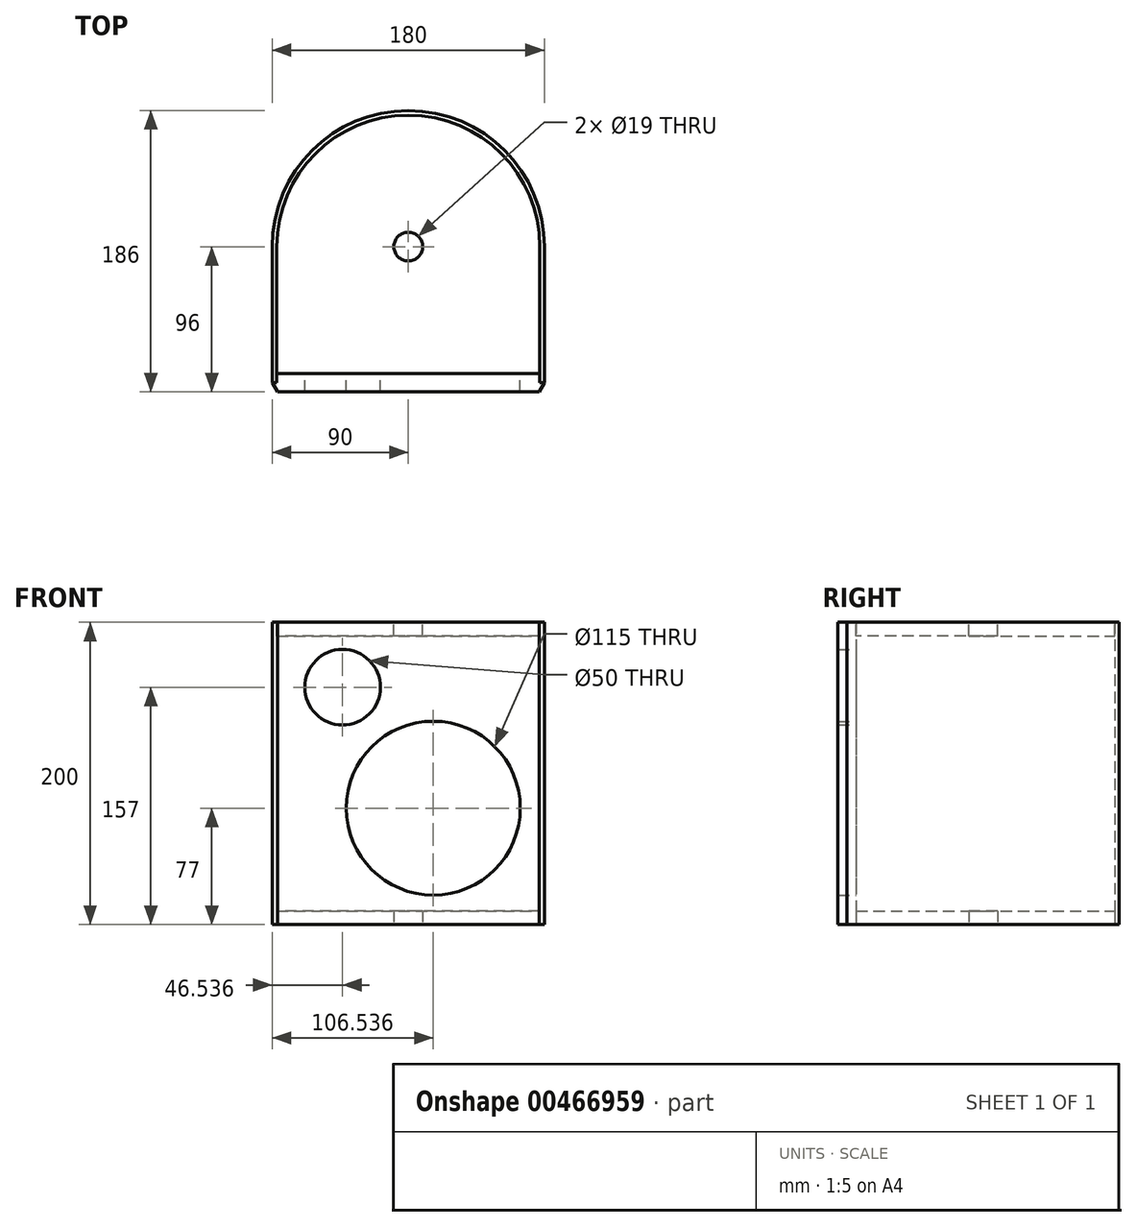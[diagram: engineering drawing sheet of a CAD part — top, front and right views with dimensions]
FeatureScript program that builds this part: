
annotation { "Feature Type Name" : "Feature", "Feature Type Description" : "" }
export const myFeature = defineFeature(function(context is Context, id is Id, definition is map)
    precondition{}
    {
        {
            var Q0;
            Q0=qCreatedBy(makeId("Top.planeOp"),FACE);
            var sketch = newSketch(context, id + "F0", { "sketchPlane" : qUnion([Q0])});
            skArc(sketch, "E0", {"start": v(90, 0) * mm, "mid": v(0, 90) * mm, "end": v(-90, 0) * mm});
            skLineSegment(sketch, "E1", {"start": v(-90, 0) * mm, "end": v(-90, -90) * mm});
            skLineSegment(sketch, "E2", {"start": v(-90, -90) * mm, "end": v(90, -90) * mm});
            skLineSegment(sketch, "E3", {"start": v(90, -90) * mm, "end": v(90, 0) * mm});
            skSolve(sketch);
        }
        {
            var Q0;
            Q0 = qSketchRegion(id + "F0", true);
            extrude(context, id + "F1", {"entities" : qUnion([Q0]), "depth" : 200 * mm});
        }
        {
            var Q0;
            Q0=makeQuery(id+"F1.opExtrude","CAP_FACE",FACE,{"disambiguationData":[OSD([sQuery(id+"F0.wireOp",EDGE,"E0"),sQuery(id+"F0.wireOp",EDGE,"E1"),sQuery(id+"F0.wireOp",EDGE,"E2"),sQuery(id+"F0.wireOp",EDGE,"E3")])],"isStart":false});
            var Q1;
            Q1=makeQuery(id+"F1.opExtrude","SWEPT_FACE",FACE,{"disambiguationData":[OSD([sQuery(id+"F0.wireOp",EDGE,"E2")])]});
            var Q2;
            Q2=makeQuery(id+"F1.opExtrude","CAP_FACE",FACE,{"disambiguationData":[OSD([sQuery(id+"F0.wireOp",EDGE,"E0"),sQuery(id+"F0.wireOp",EDGE,"E1"),sQuery(id+"F0.wireOp",EDGE,"E2"),sQuery(id+"F0.wireOp",EDGE,"E3")])],"isStart":true});
            shell(context, id + "F2", {"entities" : qUnion([Q0, Q1, Q2]), "thickness" : 3 * mm});
        }
        {
            var Q0;
            Q0=qCreatedBy(makeId("Top.planeOp"),FACE);
            var sketch = newSketch(context, id + "F3", { "sketchPlane" : qUnion([Q0])});
            skLineSegment(sketch, "E4", {"start": v(-87, -84) * mm, "end": v(87, -84) * mm});
            skLineSegment(sketch, "E5", {"start": v(87, -84) * mm, "end": v(87, -90) * mm});
            skLineSegment(sketch, "E6", {"start": v(87, -90) * mm, "end": v(90, -90) * mm});
            skLineSegment(sketch, "E7", {"start": v(90, -90) * mm, "end": v(86.54, -96) * mm});
            skLineSegment(sketch, "E8", {"start": v(86.54, -96) * mm, "end": v(-86.54, -96) * mm});
            skLineSegment(sketch, "E9", {"start": v(-86.54, -96) * mm, "end": v(-90, -90) * mm});
            skLineSegment(sketch, "E10", {"start": v(-90, -90) * mm, "end": v(-87, -90) * mm});
            skLineSegment(sketch, "E11", {"start": v(-87, -90) * mm, "end": v(-87, -84) * mm});
            skSolve(sketch);
        }
        {
            var Q0;
            Q0 = qSketchRegion(id + "F3", true);
            var Q1;
            Q1=makeQuery(id+"F1.opExtrude","CAP_FACE",FACE,{"disambiguationData":[OSD([sQuery(id+"F0.wireOp",EDGE,"E0"),sQuery(id+"F0.wireOp",EDGE,"E1"),sQuery(id+"F0.wireOp",EDGE,"E2"),sQuery(id+"F0.wireOp",EDGE,"E3")])],"isStart":false});
            extrude(context, id + "F4", {"entities" : qUnion([Q0]), "endBound" : BoundingType.UP_TO_SURFACE, "endBoundEntityFace" : qUnion([Q1]), "depth" : 25 * mm});
        }
        {
            var Q0;
            Q0=qCreatedBy(makeId("Front.planeOp"),FACE);
            var sketch = newSketch(context, id + "F5", { "sketchPlane" : qUnion([Q0])});
            skCircle(sketch, "E12", {"center": v(16.54, 77) * mm, "radius": 57.5 * mm});
            skCircle(sketch, "E13", {"center": v(-43.46, 157) * mm, "radius": 25 * mm});
            skSolve(sketch);
        }
        {
            var Q0;
            Q0 = qSketchRegion(id + "F5", true);
            extrude(context, id + "F6", {"entities" : qUnion([Q0]), "operationType" : NewBodyOperationType.REMOVE, "endBound" : BoundingType.THROUGH_ALL, "depth" : 25 * mm});
        }
        {
            var Q0;
            Q0=makeQuery(id+"F4.opExtrude","CAP_FACE",FACE,{"disambiguationData":[OSD([sQuery(id+"F3.wireOp",EDGE,"E4"),sQuery(id+"F3.wireOp",EDGE,"E5"),sQuery(id+"F3.wireOp",EDGE,"E6"),sQuery(id+"F3.wireOp",EDGE,"E7"),sQuery(id+"F3.wireOp",EDGE,"E8"),sQuery(id+"F3.wireOp",EDGE,"E9"),sQuery(id+"F3.wireOp",EDGE,"E10"),sQuery(id+"F3.wireOp",EDGE,"E11")])],"isStart":false});
            var sketch = newSketch(context, id + "F7", { "sketchPlane" : qUnion([Q0])});
            skLineSegment(sketch, "E14.0", {"start": v(-87, 0) * mm, "end": v(-87, -84) * mm});
            skArc(sketch, "E15.0", {"start": v(87, 0) * mm, "mid": v(0, 87) * mm, "end": v(-87, 0) * mm});
            skLineSegment(sketch, "E16.0", {"start": v(87, -84) * mm, "end": v(87, 0) * mm});
            skLineSegment(sketch, "E17.0", {"start": v(-87, -84) * mm, "end": v(87, -84) * mm});
            skPoint(sketch, "E18.orphan", {"position": v(-87, -90) * mm});
            skPoint(sketch, "E19.orphan", {"position": v(87, -90) * mm});
            skCircle(sketch, "E20", {"center": v(0, 0) * mm, "radius": 9.5 * mm});
            skSolve(sketch);
        }
        {
            var Q0;
            Q0 = qSketchRegion(id + "F7", true);
            extrude(context, id + "F8", {"entities" : qUnion([Q0]), "oppositeDirection" : true, "depth" : 9 * mm});
        }
        {
            var Q0;
            Q0=qCreatedBy(makeId("Top.planeOp"),FACE);
            var sketch = newSketch(context, id + "F9", { "sketchPlane" : qUnion([Q0])});
            skLineSegment(sketch, "E21.0", {"start": v(87, -84) * mm, "end": v(87, 0) * mm});
            skArc(sketch, "E22.0", {"start": v(87, 0) * mm, "mid": v(0, 87) * mm, "end": v(-87, 0) * mm});
            skLineSegment(sketch, "E22.1", {"start": v(-87, 0) * mm, "end": v(-87, -84) * mm});
            skLineSegment(sketch, "E22.2", {"start": v(-87, -84) * mm, "end": v(87, -84) * mm});
            skCircle(sketch, "E23.0", {"center": v(0, 0) * mm, "radius": 9.5 * mm});
            skSolve(sketch);
        }
        {
            var Q0;
            Q0 = qSketchRegion(id + "F9", true);
            extrude(context, id + "F10", {"entities" : qUnion([Q0]), "depth" : 9 * mm});
        }
    });
